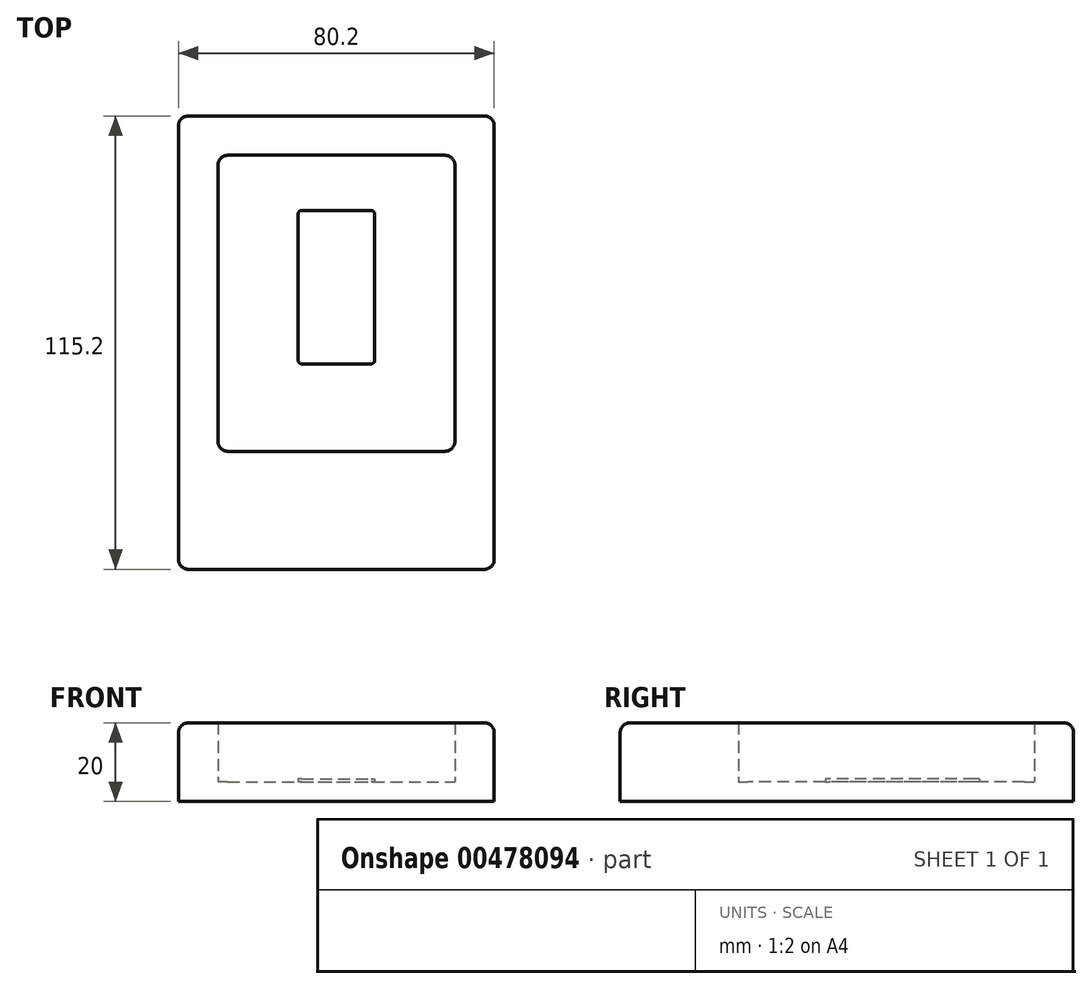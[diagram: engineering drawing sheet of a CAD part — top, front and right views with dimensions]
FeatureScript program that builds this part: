
annotation { "Feature Type Name" : "Feature", "Feature Type Description" : "" }
export const myFeature = defineFeature(function(context is Context, id is Id, definition is map)
    precondition{}
    {
        {
            var Q0;
            Q0=qCreatedBy(makeId("Top.planeOp"),FACE);
            var sketch = newSketch(context, id + "F0", { "sketchPlane" : qUnion([Q0])});
            skLineSegment(sketch, "E0.bottom", {"start": v(-30.1, 37.6) * mm, "end": v(30.1, 37.6) * mm});
            skLineSegment(sketch, "E0.top", {"start": v(-30.1, -37.6) * mm, "end": v(30.1, -37.6) * mm});
            skLineSegment(sketch, "E0.left", {"start": v(-30.1, 37.6) * mm, "end": v(-30.1, -37.6) * mm});
            skLineSegment(sketch, "E0.right", {"start": v(30.1, 37.6) * mm, "end": v(30.1, -37.6) * mm});
            skLineSegment(sketch, "E1.bottom", {"start": v(-40.1, 47.6) * mm, "end": v(40.1, 47.6) * mm});
            skLineSegment(sketch, "E1.top", {"start": v(-40.1, -67.6) * mm, "end": v(40.1, -67.6) * mm});
            skLineSegment(sketch, "E1.left", {"start": v(-40.1, 47.6) * mm, "end": v(-40.1, -67.6) * mm});
            skLineSegment(sketch, "E1.right", {"start": v(40.1, 47.6) * mm, "end": v(40.1, -67.6) * mm});
            skLineSegment(sketch, "E2.bottom", {"start": v(-9.75, 23.6) * mm, "end": v(9.75, 23.6) * mm});
            skLineSegment(sketch, "E2.top", {"start": v(-9.75, -15.4) * mm, "end": v(9.75, -15.4) * mm});
            skLineSegment(sketch, "E2.left", {"start": v(-9.75, 23.6) * mm, "end": v(-9.75, -15.4) * mm});
            skLineSegment(sketch, "E2.right", {"start": v(9.75, 23.6) * mm, "end": v(9.75, -15.4) * mm});
            skSolve(sketch);
        }
        {
            var Q0;
            Q0=makeQuery(id+"F0.imprint","IMPRINT",FACE,{"disambiguationData":[TD([[makeQuery(id+"F0.imprint","IMPRINT",EDGE,{"derivedFrom":sQuery(id+"F0.wireOp",EDGE,"E0.bottom")}),1.0]])]});
            extrude(context, id + "F1", {"entities" : qUnion([Q0]), "depth" : 20 * mm});
        }
        {
            var Q0;
            Q0=makeQuery(id+"F0.imprint","IMPRINT",FACE,{"disambiguationData":[TD([[makeQuery(id+"F0.imprint","IMPRINT",EDGE,{"derivedFrom":sQuery(id+"F0.wireOp",EDGE,"E0.bottom")}),-1.0]])]});
            extrude(context, id + "F2", {"entities" : qUnion([Q0]), "operationType" : NewBodyOperationType.ADD, "depth" : 5 * mm});
        }
        {
            var Q0;
            Q0=makeQuery(id+"F1.opExtrude","SWEPT_EDGE",EDGE,{"disambiguationData":[OSD([sQuery(id+"F0.wireOp",EDGE,"E0.bottom"),sQuery(id+"F0.wireOp",EDGE,"E0.left")])]});
            var Q1;
            Q1=makeQuery(id+"F1.opExtrude","SWEPT_EDGE",EDGE,{"disambiguationData":[OSD([sQuery(id+"F0.wireOp",EDGE,"E0.bottom"),sQuery(id+"F0.wireOp",EDGE,"E0.right")])]});
            var Q2;
            Q2=makeQuery(id+"F1.opExtrude","SWEPT_EDGE",EDGE,{"disambiguationData":[OSD([sQuery(id+"F0.wireOp",EDGE,"E0.top"),sQuery(id+"F0.wireOp",EDGE,"E0.left")])]});
            var Q3;
            Q3=makeQuery(id+"F1.opExtrude","SWEPT_EDGE",EDGE,{"disambiguationData":[OSD([sQuery(id+"F0.wireOp",EDGE,"E0.top"),sQuery(id+"F0.wireOp",EDGE,"E0.right")])]});
            fillet(context, id + "F3", {"entities" : qUnion([Q0, Q1, Q2, Q3]), "radius" : 2.5 * mm, "tangentPropagation" : true, "allowEdgeOverflow" : false});
        }
        {
            var Q0;
            Q0=makeQuery(id+"F1.opExtrude","SWEPT_EDGE",EDGE,{"disambiguationData":[OSD([sQuery(id+"F0.wireOp",EDGE,"E1.top"),sQuery(id+"F0.wireOp",EDGE,"E1.left")])]});
            var Q1;
            Q1=makeQuery(id+"F1.opExtrude","SWEPT_EDGE",EDGE,{"disambiguationData":[OSD([sQuery(id+"F0.wireOp",EDGE,"E1.top"),sQuery(id+"F0.wireOp",EDGE,"E1.right")])]});
            var Q2;
            Q2=makeQuery(id+"F1.opExtrude","SWEPT_EDGE",EDGE,{"disambiguationData":[OSD([sQuery(id+"F0.wireOp",EDGE,"E1.bottom"),sQuery(id+"F0.wireOp",EDGE,"E1.right")])]});
            var Q3;
            Q3=makeQuery(id+"F1.opExtrude","SWEPT_EDGE",EDGE,{"disambiguationData":[OSD([sQuery(id+"F0.wireOp",EDGE,"E1.bottom"),sQuery(id+"F0.wireOp",EDGE,"E1.left")])]});
            var Q4;
            Q4=makeQuery(id+"F1.opExtrude","CAP_EDGE",EDGE,{"disambiguationData":[OSD([sQuery(id+"F0.wireOp",EDGE,"E1.right")])],"isStart":false});
            var Q5;
            Q5=makeQuery(id+"F1.opExtrude","CAP_EDGE",EDGE,{"disambiguationData":[OSD([sQuery(id+"F0.wireOp",EDGE,"E1.top")])],"isStart":false});
            var Q6;
            Q6=makeQuery(id+"F1.opExtrude","CAP_EDGE",EDGE,{"disambiguationData":[OSD([sQuery(id+"F0.wireOp",EDGE,"E1.bottom")])],"isStart":false});
            var Q7;
            Q7=makeQuery(id+"F1.opExtrude","CAP_EDGE",EDGE,{"disambiguationData":[OSD([sQuery(id+"F0.wireOp",EDGE,"E1.left")])],"isStart":false});
            fillet(context, id + "F4", {"entities" : qUnion([Q0, Q1, Q2, Q3, Q4, Q5, Q6, Q7]), "radius" : 2.5 * mm, "tangentPropagation" : true, "allowEdgeOverflow" : false});
        }
        {
            var Q0;
            Q0=makeQuery(id+"F0.imprint","IMPRINT",FACE,{"disambiguationData":[TD([[makeQuery(id+"F0.imprint","IMPRINT",EDGE,{"derivedFrom":sQuery(id+"F0.wireOp",EDGE,"E2.bottom")}),-1.0]])]});
            extrude(context, id + "F5", {"entities" : qUnion([Q0]), "operationType" : NewBodyOperationType.ADD, "depth" : 5.7 * mm});
        }
        {
            var Q0;
            Q0=makeQuery(id+"F5.opExtrude","SWEPT_EDGE",EDGE,{"disambiguationData":[OSD([sQuery(id+"F0.wireOp",EDGE,"E2.top"),sQuery(id+"F0.wireOp",EDGE,"E2.left")])]});
            var Q1;
            Q1=makeQuery(id+"F5.opExtrude","SWEPT_EDGE",EDGE,{"disambiguationData":[OSD([sQuery(id+"F0.wireOp",EDGE,"E2.top"),sQuery(id+"F0.wireOp",EDGE,"E2.right")])]});
            var Q2;
            Q2=makeQuery(id+"F5.opExtrude","SWEPT_EDGE",EDGE,{"disambiguationData":[OSD([sQuery(id+"F0.wireOp",EDGE,"E2.bottom"),sQuery(id+"F0.wireOp",EDGE,"E2.right")])]});
            var Q3;
            Q3=makeQuery(id+"F5.opExtrude","SWEPT_EDGE",EDGE,{"disambiguationData":[OSD([sQuery(id+"F0.wireOp",EDGE,"E2.bottom"),sQuery(id+"F0.wireOp",EDGE,"E2.left")])]});
            fillet(context, id + "F6", {"entities" : qUnion([Q0, Q1, Q2, Q3]), "radius" : 1 * mm, "tangentPropagation" : true, "allowEdgeOverflow" : false});
        }
    });
